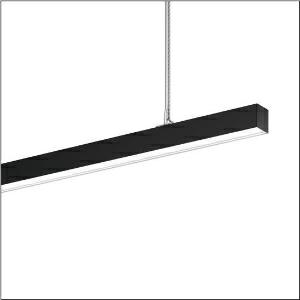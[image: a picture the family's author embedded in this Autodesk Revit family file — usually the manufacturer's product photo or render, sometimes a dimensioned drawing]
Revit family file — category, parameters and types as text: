
# Revit family: silica_r__21_51mx30tat4b_500a
name_source: partatom
category: Lighting Fixtures
units: mm (PartAtom-declared; Revit-internal decimal feet)

## family parameters
Cut with Voids When Loaded = No
Host = Face
Light Source = No
Part Type = Normal
Room Calculation Point = No
Round Connector Dimension = Use Diameter
Shared = No

## types (1)
- --- (1 x LED, 4120 lm, 33.8 W, 6500K)
    Apparent Load = 34 VA
    CIE Flux Codes = 47 79 96 58 100
    Color Rendering = 80
    Color Temperature = 6500K
    Default Elevation = 1800 mm
    Description = Silica® 21, office luminaire, primary optical cover: cover, of PMMA, opal, light emission: direct/indirect distribution, primary light characteristic: symmetric, installation type: suspended mounting, LED, rated luminous flux: 4.120lm, luminous efficacy: 116lm/W, light colour: 8tw, colour temperature: 2700..6500K, control gear: ECG DALI, with terminal, 3+2-pole, max. 2.5mm², mains connection: 220..240V, AC, 50/60Hz, rated input power: 35.5W, luminaire housing, of aluminium, jet black (RAL 9005), length: 1.204mm, width: 53mm, height: 53mm, protection rating (complete): IP20, insulation class (complete): insulation class I (protective earthing), certification: CE, permissible operating ambient temperature: 0..+35°C, standard: EN 50419, packaging unit: 1 piece
    Height = 53 mm
    Lamp = 1 x LED
    Lamp Light Flux = 4120 lm
    Lamp Power = 33.8 W
    Lamp count = 1
    Length = 1204 mm
    Luminous efficacy = 122 lm/W
    Manufacturer = Siteco
    ModVariant = No
    Model = 51MX30TAT4B
    Mounting Place = Ceiling
    Mounting Type = Pendant
    Number of Poles = 1
    OnlyDefault = Yes
    Power Factor = 1
    Product Name = Silica® 21
    Product group = office luminaire | ceiling pendant
    ProductGroupID = 902
    Protection Class = Protection class I
    Protection Degree = IP 20
    RLX_Detail_Level = 1
    RLX_Emergency_Light_Flux = 0 lm
    RLX_Emergency_Type = 0
    RLX_Emergency_Type_DB = No
    RlxData = <blob elided: 22853 chars, md5=4dbea30a>
    Socket = socket
    Standby Power = 0 W
    System Light Flux = 4120 lm
    System Power = 34 W
    Type Comments = individual setting
    Type Image = l_1297744.jpg
    URL = http://relux.com
    VarID = @adj_070963
    Voltage = 0 V
    Weight = 0.00 kg
    Width = 53 mm

## geometry (parser evidence)
native form markers: Blend x4, Sweep x12
no freeform markers — native parametric forms only
